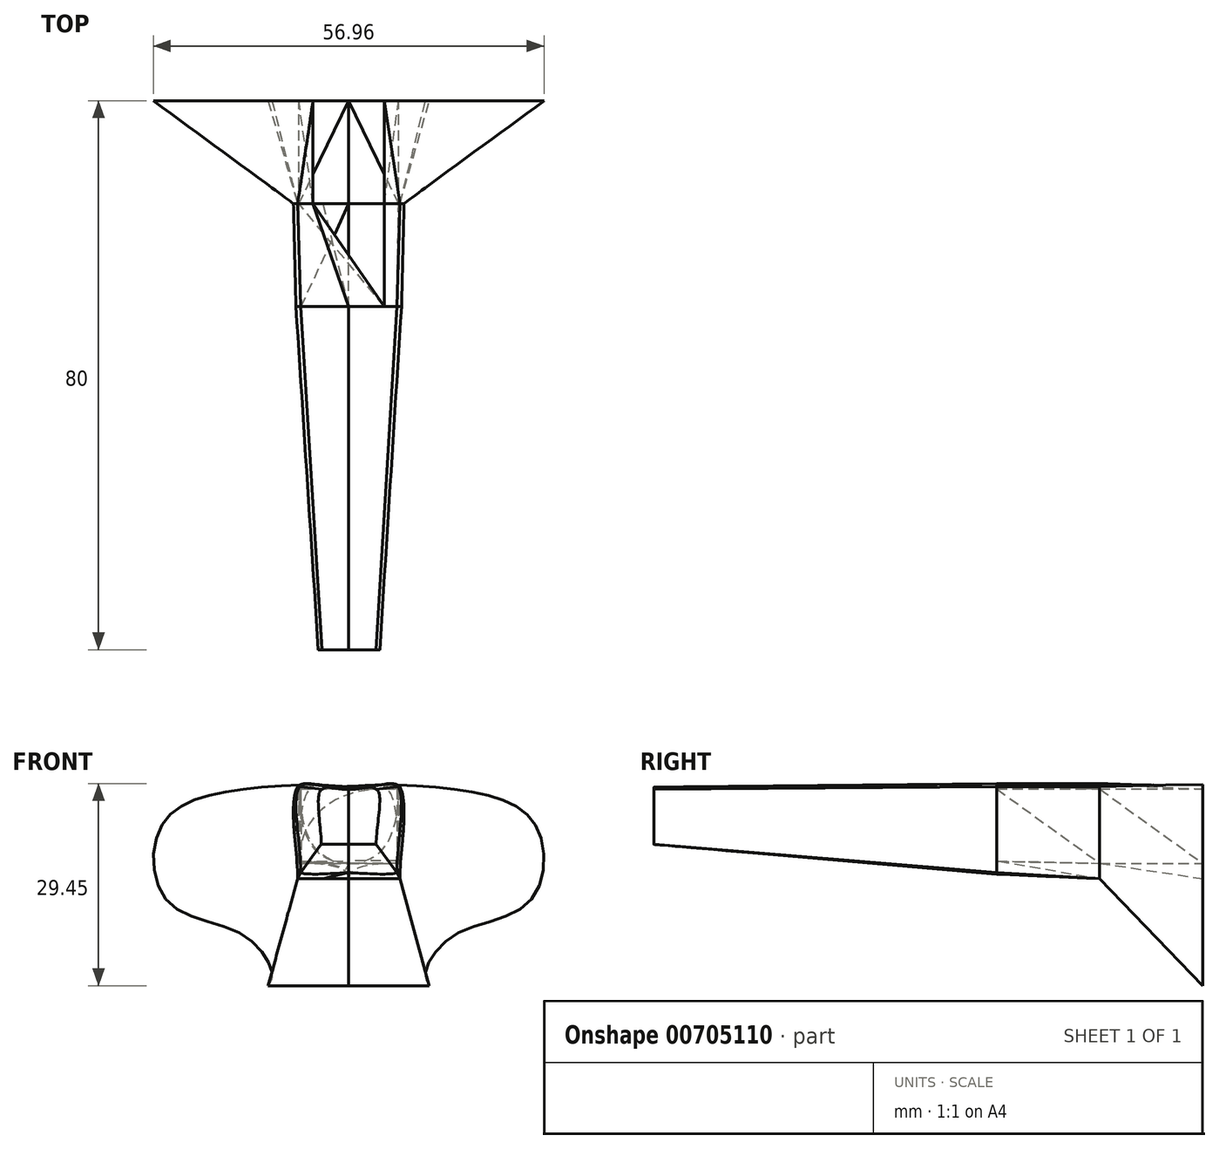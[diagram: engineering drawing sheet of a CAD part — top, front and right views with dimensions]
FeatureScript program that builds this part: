
annotation { "Feature Type Name" : "Feature", "Feature Type Description" : "" }
export const myFeature = defineFeature(function(context is Context, id is Id, definition is map)
    precondition{}
    {
        {
            var Q0;
            Q0=qCreatedBy(makeId("Front.planeOp"),FACE);
            var sketch = newSketch(context, id + "F0", { "sketchPlane" : qUnion([Q0])});
            skLineSegment(sketch, "E0", {"start": v(0, 38.05) * mm, "end": v(0, 46.05) * mm});
            skFitSpline(sketch, "E1", {"points": [v(0, 46.05) * mm, v(4, 46.05) * mm], "startDerivative": vector(8, 0) * mm, "endDerivative": vector(2.44, -2.23) * mm});
            skFitSpline(sketch, "E2", {"points": [v(0, 38.05) * mm, v(4, 38.05) * mm], "startDerivative": vector(8, 0) * mm, "endDerivative": vector(8, 0) * mm});
            skFitSpline(sketch, "E3", {"points": [v(4, 46.05) * mm, v(4, 38.05) * mm], "startDerivative": vector(3.53, -1.04) * mm, "endDerivative": vector(0, -8) * mm});
            skFitSpline(sketch, "E4.MirrorCS", {"points": [v(0, 46.05) * mm, v(-3.88, 46.04) * mm], "startDerivative": vector(-8, 0) * mm, "endDerivative": vector(-2.44, -2.23) * mm});
            skFitSpline(sketch, "E5.MirrorCS", {"points": [v(-3.88, 46.04) * mm, v(-4, 38.04) * mm], "startDerivative": vector(-3.53, -1.04) * mm, "endDerivative": vector(0, -8) * mm});
            skFitSpline(sketch, "E6.MirrorCS", {"points": [v(0, 38.05) * mm, v(-4, 38.04) * mm], "startDerivative": vector(-8, 0) * mm, "endDerivative": vector(-8, 0) * mm});
            skSolve(sketch);
        }
        {
            var Q0;
            Q0=qCreatedBy(makeId("Front.planeOp"),FACE);
            cPlane(context, id + "F1", {"entities" : qUnion([Q0]), "cplaneType" : CPlaneType.OFFSET, "offset" : 50 * mm, "oppositeDirection" : true, "width" : 150 * mm, "height" : 150 * mm});
        }
        {
            var Q0;
            Q0=qCreatedBy(id+"F1.planeOp",FACE);
            var sketch = newSketch(context, id + "F2", { "sketchPlane" : qUnion([Q0])});
            skLineSegment(sketch, "E7", {"start": v(0, 46.47) * mm, "end": v(0, 33.9) * mm});
            skFitSpline(sketch, "E8", {"points": [v(0, 46.47) * mm, v(-7, 46.47) * mm], "startDerivative": vector(-12.4, -0.93) * mm, "endDerivative": vector(-1.45, -3.11) * mm});
            skFitSpline(sketch, "E9", {"points": [v(-7, 46.47) * mm, v(-7, 33.9) * mm], "startDerivative": vector(-4.77, -1.35) * mm, "endDerivative": vector(-0.2, -9.75) * mm});
            skFitSpline(sketch, "E10", {"points": [v(0, 33.9) * mm, v(-7, 33.9) * mm], "startDerivative": vector(-4.44, 0) * mm, "endDerivative": vector(-3.42, 1.35) * mm});
            skFitSpline(sketch, "E11.MirrorCS", {"points": [v(0, 46.47) * mm, v(7, 46.47) * mm], "startDerivative": vector(12.4, -0.93) * mm, "endDerivative": vector(1.45, -3.11) * mm});
            skFitSpline(sketch, "E12.MirrorCS", {"points": [v(7, 46.47) * mm, v(7, 33.9) * mm], "startDerivative": vector(4.77, -1.35) * mm, "endDerivative": vector(0.2, -9.75) * mm});
            skFitSpline(sketch, "E13.MirrorCS", {"points": [v(0, 33.9) * mm, v(7, 33.9) * mm], "startDerivative": vector(4.44, 0) * mm, "endDerivative": vector(3.42, 1.35) * mm});
            skSolve(sketch);
        }
        {
            var Q0;
            Q0=makeQuery(id+"F0.imprint","IMPRINT",FACE,{"disambiguationData":[TD([[makeQuery(id+"F0.imprint","IMPRINT",EDGE,{"derivedFrom":sQuery(id+"F0.wireOp",EDGE,"E0")}),1.0]])]});
            var Q1;
            Q1=makeQuery(id+"F2.imprint","IMPRINT",FACE,{"disambiguationData":[TD([[makeQuery(id+"F2.imprint","IMPRINT",EDGE,{"derivedFrom":sQuery(id+"F2.wireOp",EDGE,"E7")}),-1.0]])]});
            loft(context, id + "F3", {"sheetProfilesArray" : [{ "sheetProfileEntities" : qUnion([Q0]) }, { "sheetProfileEntities" : qUnion([Q1]) }]});
        }
        {
            var Q1;
            Q1=makeQuery(id+"F0.imprint","IMPRINT",FACE,{"disambiguationData":[TD([[makeQuery(id+"F0.imprint","IMPRINT",EDGE,{"derivedFrom":sQuery(id+"F0.wireOp",EDGE,"E0")}),-1.0]])]});
            var Q2;
            Q2=makeQuery(id+"F2.imprint","IMPRINT",FACE,{"disambiguationData":[TD([[makeQuery(id+"F2.imprint","IMPRINT",EDGE,{"derivedFrom":sQuery(id+"F2.wireOp",EDGE,"E7")}),1.0]])]});
            loft(context, id + "F4", {"sheetProfilesArray" : [{ "sheetProfileEntities" : qUnion([Q1]) }, { "sheetProfileEntities" : qUnion([Q2]) }]});
        }
        {
            var Q0;
            Q0=qCreatedBy(id+"F1.planeOp",FACE);
            var sketch = newSketch(context, id + "F5", { "sketchPlane" : qUnion([Q0])});
            skPoint(sketch, "E14", {"position": v(0, 46.47) * mm});
            skPoint(sketch, "E15", {"position": v(-7, 46.47) * mm});
            skPoint(sketch, "E16", {"position": v(7, 46.47) * mm});
            skFitSpline(sketch, "E17", {"points": [v(0, 46.47) * mm, v(-7, 46.47) * mm], "startDerivative": vector(-12.4, -0.93) * mm, "endDerivative": vector(-1.45, -3.11) * mm});
            skFitSpline(sketch, "E18", {"points": [v(-7, 46.47) * mm, v(-7, 33.9) * mm], "startDerivative": vector(-4.77, -1.35) * mm, "endDerivative": vector(-0.2, -9.75) * mm});
            skFitSpline(sketch, "E19", {"points": [v(0, 33.9) * mm, v(-7, 33.9) * mm], "startDerivative": vector(-4.44, 0) * mm, "endDerivative": vector(-3.42, 1.35) * mm});
            skFitSpline(sketch, "E20.MirrorCS", {"points": [v(0, 46.47) * mm, v(7, 46.47) * mm], "startDerivative": vector(12.4, -0.93) * mm, "endDerivative": vector(1.45, -3.11) * mm});
            skFitSpline(sketch, "E21.MirrorCS", {"points": [v(7, 46.47) * mm, v(7, 33.9) * mm], "startDerivative": vector(4.77, -1.35) * mm, "endDerivative": vector(0.2, -9.75) * mm});
            skFitSpline(sketch, "E22.MirrorCS", {"points": [v(0, 33.9) * mm, v(7, 33.9) * mm], "startDerivative": vector(4.44, 0) * mm, "endDerivative": vector(3.42, 1.35) * mm});
            skLineSegment(sketch, "E23", {"start": v(0, 46.1) * mm, "end": v(-7, 46.1) * mm});
            skLineSegment(sketch, "E24", {"start": v(-7, 46.1) * mm, "end": v(-6.93, 35.58) * mm});
            skLineSegment(sketch, "E25", {"start": v(-6.93, 35.58) * mm, "end": v(0, 35.63) * mm});
            skLineSegment(sketch, "E26", {"start": v(0, 46.1) * mm, "end": v(7, 46.1) * mm});
            skLineSegment(sketch, "E27", {"start": v(7, 46.1) * mm, "end": v(7, 35.63) * mm});
            skLineSegment(sketch, "E28", {"start": v(7, 35.63) * mm, "end": v(0, 35.63) * mm});
            skLineSegment(sketch, "E29", {"start": v(5.2, 46.1) * mm, "end": v(5.2, 46.79) * mm});
            skLineSegment(sketch, "E30.MirrorCS", {"start": v(-5.2, 46.1) * mm, "end": v(-5.2, 46.79) * mm});
            skLineSegment(sketch, "E31", {"start": v(0, 35.63) * mm, "end": v(0, 33.9) * mm});
            skSolve(sketch);
        }
        {
            var Q0;
            Q0=qCreatedBy(id+"F1.planeOp",FACE);
            cPlane(context, id + "F6", {"entities" : qUnion([Q0]), "cplaneType" : CPlaneType.OFFSET, "offset" : 15 * mm, "oppositeDirection" : true, "width" : 150 * mm, "height" : 150 * mm});
        }
        {
            var Q0;
            Q0=qCreatedBy(id+"F6.planeOp",FACE);
            var sketch = newSketch(context, id + "F7", { "sketchPlane" : qUnion([Q0])});
            skLineSegment(sketch, "E32", {"start": v(5.2, 46.1) * mm, "end": v(5.2, 46.79) * mm});
            skFitSpline(sketch, "E33", {"points": [v(5.2, 46.79) * mm, v(7.45, 46.47) * mm], "startDerivative": vector(2.9, 0.74) * mm, "endDerivative": vector(1.35, -1.22) * mm});
            skLineSegment(sketch, "E34", {"start": v(0, 35.3) * mm, "end": v(7.27, 35.3) * mm});
            skLineSegment(sketch, "E35", {"start": v(7.27, 35.3) * mm, "end": v(7.27, 46.1) * mm});
            skLineSegment(sketch, "E36", {"start": v(7.27, 46.1) * mm, "end": v(5.2, 46.1) * mm});
            skLineSegment(sketch, "E37", {"start": v(0, 35.3) * mm, "end": v(0, 33.05) * mm});
            skFitSpline(sketch, "E38", {"points": [v(7.45, 46.47) * mm, v(7.45, 33.05) * mm], "startDerivative": vector(4.17, -8.48) * mm, "endDerivative": vector(0, -13.41) * mm});
            skLineSegment(sketch, "E39", {"start": v(0, 33.05) * mm, "end": v(7.45, 33.05) * mm});
            skLineSegment(sketch, "E40.MirrorCS", {"start": v(-5.2, 46.1) * mm, "end": v(-5.2, 46.79) * mm});
            skLineSegment(sketch, "E41.MirrorCS", {"start": v(-7.27, 46.1) * mm, "end": v(-5.2, 46.1) * mm});
            skFitSpline(sketch, "E42.MirrorCS", {"points": [v(-5.2, 46.79) * mm, v(-7.45, 46.47) * mm], "startDerivative": vector(-2.9, 0.74) * mm, "endDerivative": vector(-1.35, -1.22) * mm});
            skFitSpline(sketch, "E43.MirrorCS", {"points": [v(-7.45, 46.47) * mm, v(-7.45, 33.05) * mm], "startDerivative": vector(-4.17, -8.48) * mm, "endDerivative": vector(0, -13.41) * mm});
            skLineSegment(sketch, "E44.MirrorCS", {"start": v(-7.27, 35.3) * mm, "end": v(-7.27, 46.1) * mm});
            skLineSegment(sketch, "E45.MirrorCS", {"start": v(0, 35.3) * mm, "end": v(-7.27, 35.3) * mm});
            skLineSegment(sketch, "E46.MirrorCS", {"start": v(0, 33.05) * mm, "end": v(-7.45, 33.05) * mm});
            skSolve(sketch);
        }
        {
            var Q1;
            {var subQ3=sQuery(id+"F5.wireOp",EDGE,"E21.MirrorCS");Q1=makeQuery(id+"F5.imprint","IMPRINT",FACE,{"disambiguationData":[TD([[makeQuery(id+"F5.imprint","IMPRINT",EDGE,{"derivedFrom":subQ3}),-1.0]])]});}
            var Q2;
            Q2=makeQuery(id+"F7.imprint","IMPRINT",FACE,{"disambiguationData":[TD([[makeQuery(id+"F7.imprint","IMPRINT",EDGE,{"derivedFrom":sQuery(id+"F7.wireOp",EDGE,"E32")}),-1.0]])]});
            loft(context, id + "F8", {"sheetProfilesArray" : [{ "sheetProfileEntities" : qUnion([Q1]) }, { "sheetProfileEntities" : qUnion([Q2]) }]});
        }
        {
            var Q0;
            {var subQ3=sQuery(id+"F5.wireOp",EDGE,"E18");Q0=makeQuery(id+"F5.imprint","IMPRINT",FACE,{"disambiguationData":[TD([[makeQuery(id+"F5.imprint","IMPRINT",EDGE,{"derivedFrom":subQ3}),1.0]])]});}
            var Q1;
            Q1=makeQuery(id+"F7.imprint","IMPRINT",FACE,{"disambiguationData":[TD([[makeQuery(id+"F7.imprint","IMPRINT",EDGE,{"derivedFrom":sQuery(id+"F7.wireOp",EDGE,"E37")}),-1.0]])]});
            loft(context, id + "F9", {"sheetProfilesArray" : [{ "sheetProfileEntities" : qUnion([Q0]) }, { "sheetProfileEntities" : qUnion([Q1]) }]});
        }
        {
            var Q0;
            Q0=qCreatedBy(id+"F6.planeOp",FACE);
            cPlane(context, id + "F10", {"entities" : qUnion([Q0]), "cplaneType" : CPlaneType.OFFSET, "offset" : 15 * mm, "oppositeDirection" : true, "width" : 150 * mm, "height" : 150 * mm});
        }
        {
            var Q0;
            Q0=qCreatedBy(id+"F10.planeOp",FACE);
            var sketch = newSketch(context, id + "F11", { "sketchPlane" : qUnion([Q0])});
            skLineSegment(sketch, "E47", {"start": v(5.2, 46.1) * mm, "end": v(7.27, 46.1) * mm});
            skLineSegment(sketch, "E48", {"start": v(7.27, 46.1) * mm, "end": v(7.27, 35.3) * mm});
            skLineSegment(sketch, "E49", {"start": v(7.27, 35.3) * mm, "end": v(0, 35.3) * mm});
            skLineSegment(sketch, "E50", {"start": v(0, 35.3) * mm, "end": v(0, 33.05) * mm});
            skLineSegment(sketch, "E51", {"start": v(5.2, 46.79) * mm, "end": v(5.2, 46.1) * mm});
            skPoint(sketch, "E52", {"position": v(0, 17.45) * mm});
            skFitSpline(sketch, "E53", {"points": [v(5.2, 46.79) * mm, v(20.72, 45.1) * mm, v(27.7, 39.97) * mm, v(26.3, 29.62) * mm, v(15.25, 24.74) * mm, v(11.18, 19.15) * mm, v(11.76, 17.45) * mm], "startDerivative": vector(72.88, -2.9) * mm, "endDerivative": vector(12.4, -19.58) * mm});
            skLineSegment(sketch, "E54", {"start": v(0, 33.05) * mm, "end": v(0, 17.45) * mm});
            skLineSegment(sketch, "E55", {"start": v(11.76, 17.45) * mm, "end": v(0, 17.45) * mm});
            skSolve(sketch);
        }
        {
            var Q1;
            Q1=makeQuery(id+"F7.imprint","IMPRINT",FACE,{"disambiguationData":[TD([[makeQuery(id+"F7.imprint","IMPRINT",EDGE,{"derivedFrom":sQuery(id+"F7.wireOp",EDGE,"E32")}),-1.0]])]});
            var Q2;
            Q2=makeQuery(id+"F11.imprint","IMPRINT",FACE,{"disambiguationData":[TD([[makeQuery(id+"F11.imprint","IMPRINT",EDGE,{"derivedFrom":sQuery(id+"F11.wireOp",EDGE,"E47")}),1.0]])]});
            loft(context, id + "F12", {"sheetProfilesArray" : [{ "sheetProfileEntities" : qUnion([Q1]) }, { "sheetProfileEntities" : qUnion([Q2]) }]});
        }
        {
            var Q0;
            Q0=makeQuery(id+"F12.opLoft","SWEPT_BODY",BODY,{"disambiguationData":[OSD([makeQuery(id+"F7.imprint","IMPRINT",FACE,{"disambiguationData":[TD([[makeQuery(id+"F7.imprint","IMPRINT",EDGE,{"derivedFrom":sQuery(id+"F7.wireOp",EDGE,"E32")}),-1.0]])]}),makeQuery(id+"F11.imprint","IMPRINT",FACE,{"disambiguationData":[TD([[makeQuery(id+"F11.imprint","IMPRINT",EDGE,{"derivedFrom":sQuery(id+"F11.wireOp",EDGE,"E47")}),1.0]])]})])]});
            var Q1;
            Q1=qCreatedBy(makeId("Right.planeOp"),FACE);
            mirror(context, id + "F13", {"entities" : qUnion([Q0]), "mirrorPlane" : qUnion([Q1])});
        }
    });
